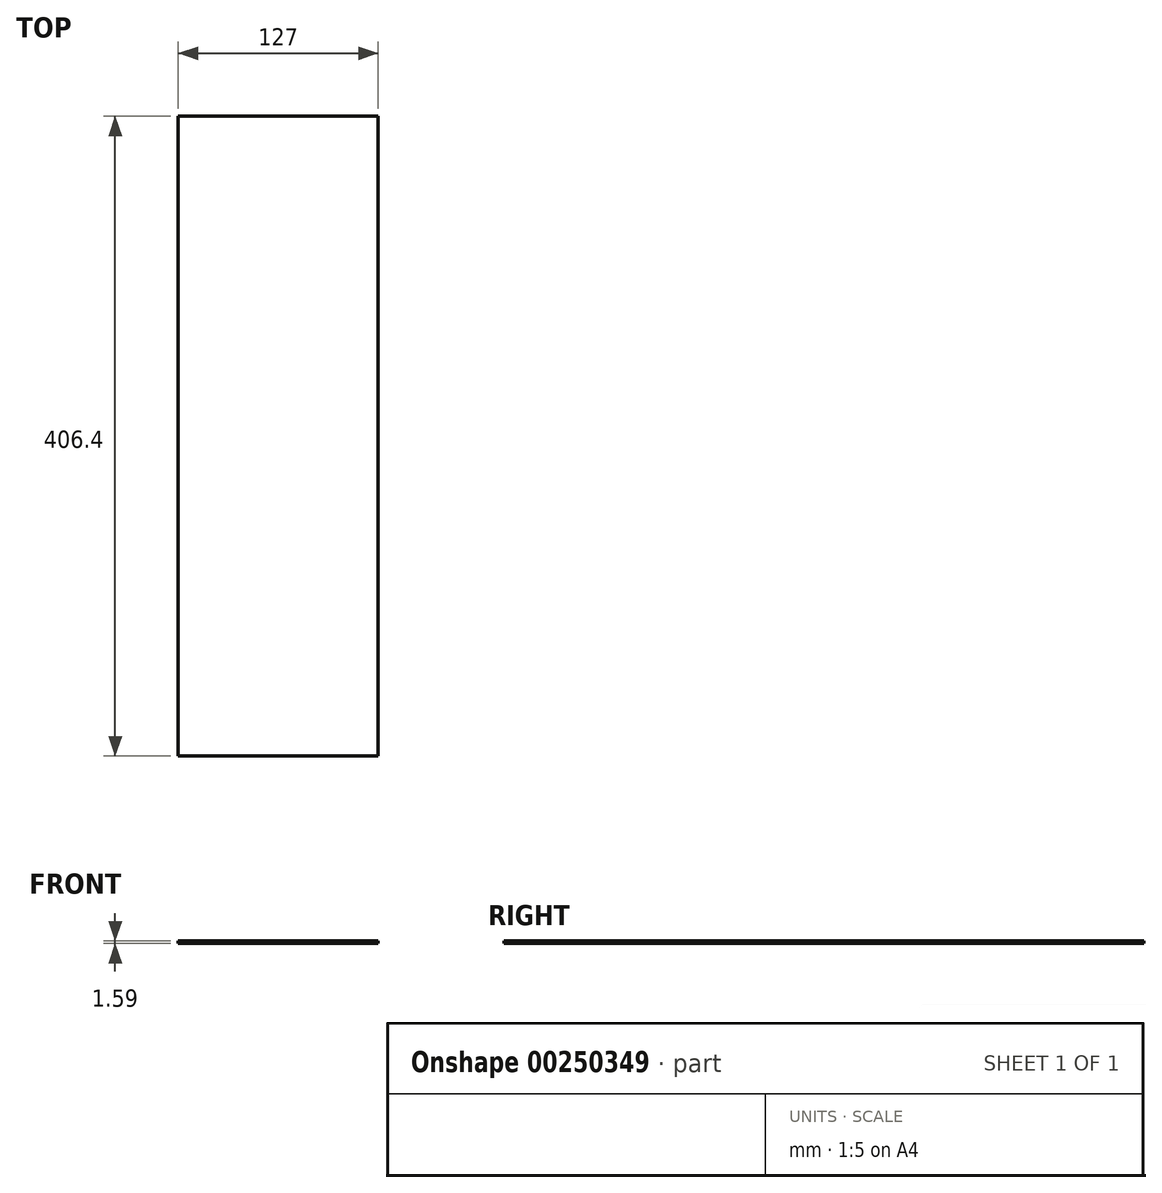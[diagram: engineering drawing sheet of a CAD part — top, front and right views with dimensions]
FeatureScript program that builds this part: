
annotation { "Feature Type Name" : "Feature", "Feature Type Description" : "" }
export const myFeature = defineFeature(function(context is Context, id is Id, definition is map)
    precondition{}
    {
        {
            var Q0;
            Q0=qCreatedBy(makeId("Top.planeOp"),FACE);
            var sketch = newSketch(context, id + "F0", { "sketchPlane" : qUnion([Q0])});
            skLineSegment(sketch, "E0.bottom", {"start": v(63.5, 203.2) * mm, "end": v(-63.5, 203.2) * mm});
            skLineSegment(sketch, "E0.top", {"start": v(63.5, -203.2) * mm, "end": v(-63.5, -203.2) * mm});
            skLineSegment(sketch, "E0.left", {"start": v(63.5, 203.2) * mm, "end": v(63.5, -203.2) * mm});
            skLineSegment(sketch, "E0.right", {"start": v(-63.5, 203.2) * mm, "end": v(-63.5, -203.2) * mm});
            skPoint(sketch, "E0.middle", {"position": v(0, 0) * mm});
            skSolve(sketch);
        }
        {
            var Q0;
            Q0 = qSketchRegion(id + "F0", true);
            extrude(context, id + "F1", {"entities" : qUnion([Q0]), "depth" : 1.59 * mm});
        }
    });
